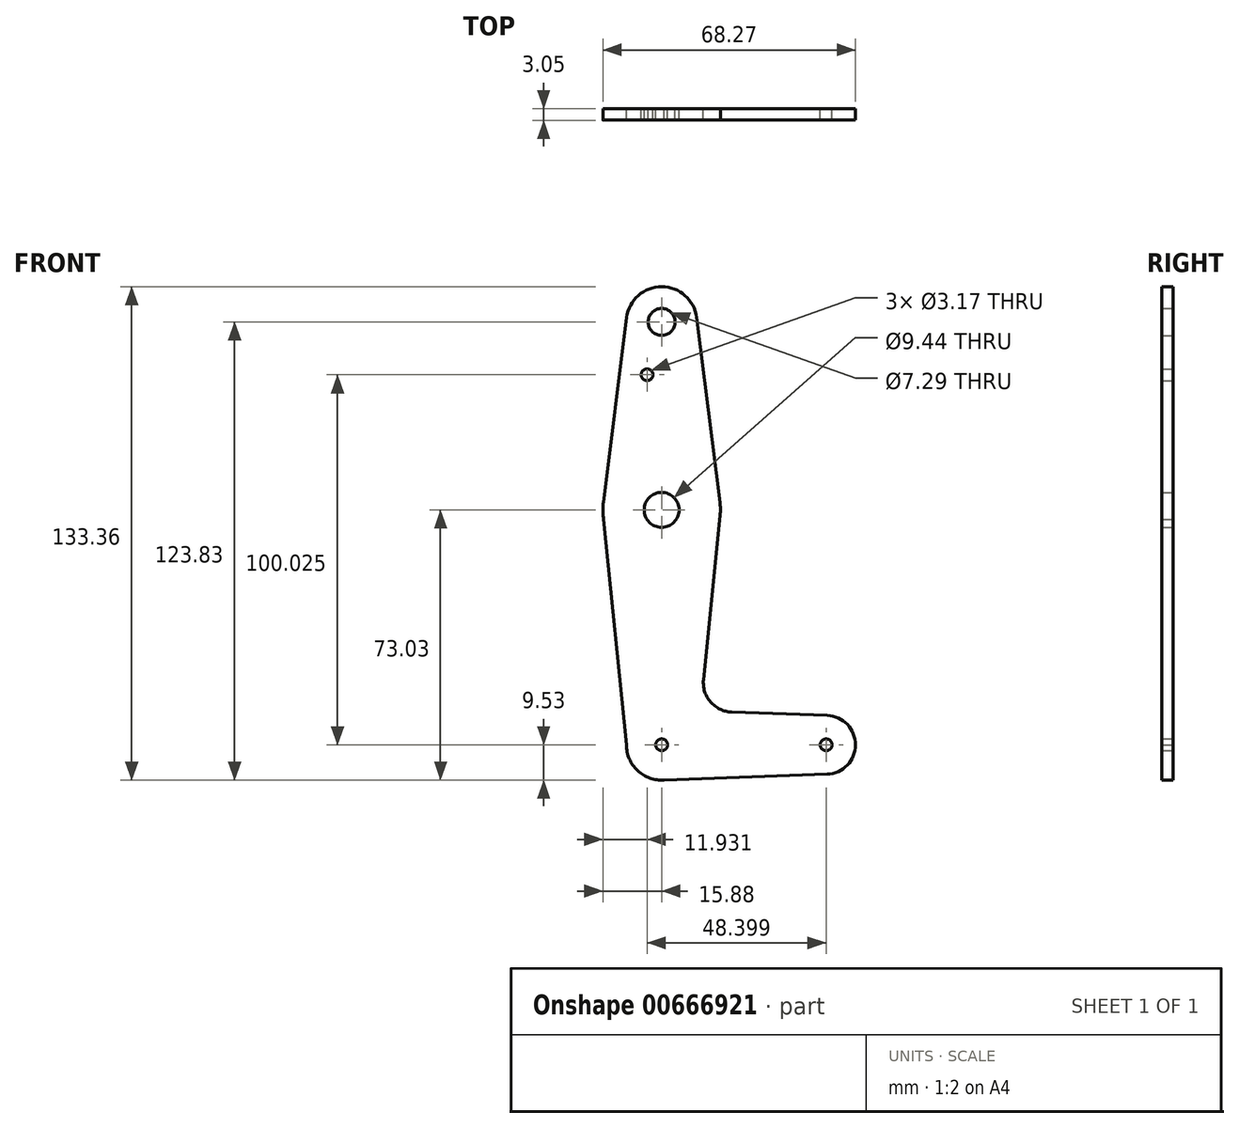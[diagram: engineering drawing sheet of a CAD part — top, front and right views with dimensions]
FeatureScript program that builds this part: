
annotation { "Feature Type Name" : "Feature", "Feature Type Description" : "" }
export const myFeature = defineFeature(function(context is Context, id is Id, definition is map)
    precondition{}
    {
        {
            var Q0;
            Q0=qCreatedBy(makeId("Front.planeOp"),FACE);
            var sketch = newSketch(context, id + "F0", { "sketchPlane" : qUnion([Q0])});
            skLineSegment(sketch, "E0", {"start": v(0, 0) * mm, "end": v(44.45, 0) * mm});
            skLineSegment(sketch, "E1", {"start": v(0, 0) * mm, "end": v(0, 114.3) * mm});
            skCircle(sketch, "E2", {"center": v(0, 63.5) * mm, "radius": 15.88 * mm});
            skCircle(sketch, "E3", {"center": v(0, 114.3) * mm, "radius": 9.53 * mm});
            skCircle(sketch, "E4", {"center": v(0, 0) * mm, "radius": 9.53 * mm});
            skCircle(sketch, "E5", {"center": v(44.45, 0) * mm, "radius": 7.94 * mm});
            skLineSegment(sketch, "E6", {"start": v(-9.45, 115.5) * mm, "end": v(-15.75, 65.48) * mm});
            skLineSegment(sketch, "E7", {"start": v(11.3, 17.6) * mm, "end": v(15.8, 61.9) * mm});
            skLineSegment(sketch, "E8", {"start": v(15.75, 65.48) * mm, "end": v(9.45, 115.5) * mm});
            skCircle(sketch, "E9", {"center": v(0, 63.5) * mm, "radius": 4.72 * mm});
            skCircle(sketch, "E10", {"center": v(0, 114.3) * mm, "radius": 3.64 * mm});
            skLineSegment(sketch, "E11", {"start": v(-9.52, 0) * mm, "end": v(-15.66, 60.92) * mm});
            skLineSegment(sketch, "E12", {"start": v(18.93, 8.85) * mm, "end": v(44.73, 7.93) * mm});
            skLineSegment(sketch, "E13", {"start": v(0, -9.53) * mm, "end": v(44.73, -7.93) * mm});
            skCircle(sketch, "E14", {"center": v(0, 0) * mm, "radius": 1.59 * mm});
            skCircle(sketch, "E15", {"center": v(0, 114.3) * mm, "radius": 1.59 * mm});
            skCircle(sketch, "E16", {"center": v(0, 63.5) * mm, "radius": 1.59 * mm});
            skCircle(sketch, "E17", {"center": v(44.45, 0) * mm, "radius": 1.59 * mm});
            skCircle(sketch, "E18", {"center": v(-3.95, 100.03) * mm, "radius": 1.59 * mm});
            skPoint(sketch, "E19.newPointB", {"position": v(0, 9.53) * mm});
            skArc(sketch, "E19.filletArc", {"start": v(11.3, 17.6) * mm, "mid": v(13.22, 11.57) * mm, "end": v(18.93, 8.85) * mm});
            skSolve(sketch);
        }
        {
            var Q0;
            Q0 = qSketchRegion(id + "F0", true);
            var Q1;
            {var subQ0=sQuery(id+"F0.wireOp",EDGE,"E14");var subQ1=sQuery(id+"F0.wireOp",EDGE,"E0");var subQ2=makeQuery(id+"F0.imprint","INTERSECT",VERTEX,{"derivedFrom":[subQ1,subQ0]});Q1=makeQuery(id+"F0.imprint","IMPRINT",FACE,{"disambiguationData":[TD([[makeQuery(id+"F0.imprint","IMPRINT",EDGE,{"disambiguationData":[TD([[subQ2,-1.0]])],"derivedFrom":subQ1}),1.0]])]});}
            extrude(context, id + "F1", {"entities" : qUnion([Q0, Q1]), "depth" : 3.05 * mm, "offsetDistance" : 25.4 * mm});
        }
    });
